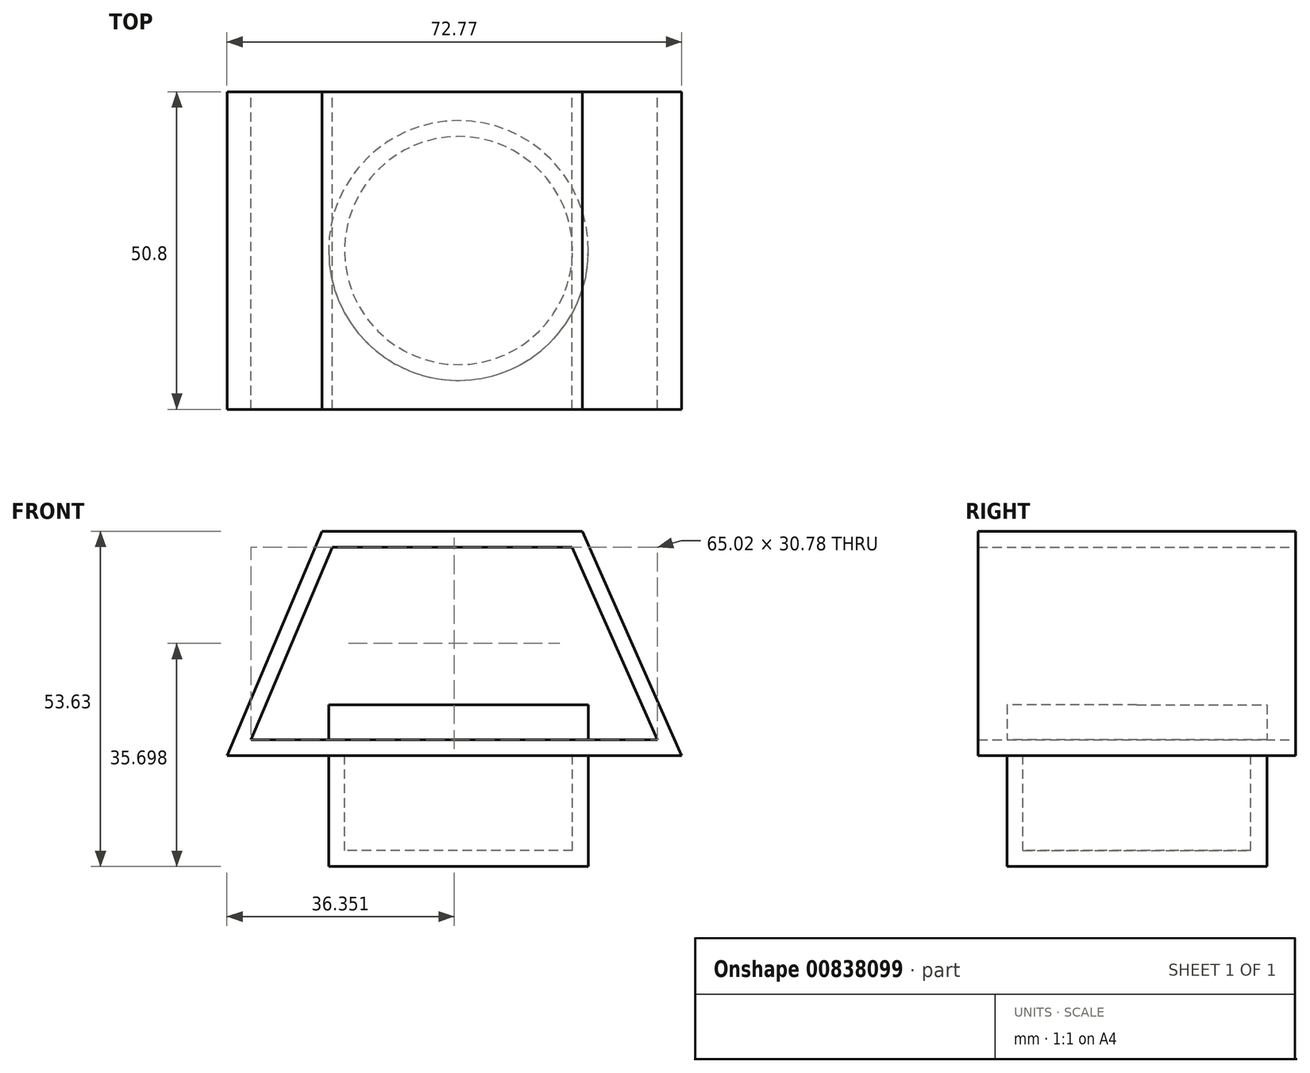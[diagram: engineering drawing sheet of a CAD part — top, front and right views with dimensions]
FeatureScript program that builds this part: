
annotation { "Feature Type Name" : "Feature", "Feature Type Description" : "" }
export const myFeature = defineFeature(function(context is Context, id is Id, definition is map)
    precondition{}
    {
        {
            var Q0;
            Q0=qCreatedBy(makeId("Front.planeOp"),FACE);
            var sketch = newSketch(context, id + "F0", { "sketchPlane" : qUnion([Q0])});
            skLineSegment(sketch, "E0", {"start": v(19.83, 35.86) * mm, "end": v(-21.85, 35.86) * mm});
            skLineSegment(sketch, "E1", {"start": v(-21.85, 35.86) * mm, "end": v(-37.05, 0) * mm});
            skLineSegment(sketch, "E2", {"start": v(19.83, 35.86) * mm, "end": v(35.72, 0) * mm});
            skLineSegment(sketch, "E3", {"start": v(35.72, 0) * mm, "end": v(0, 0) * mm});
            skLineSegment(sketch, "E4", {"start": v(0, 0) * mm, "end": v(-37.05, 0) * mm});
            skSolve(sketch);
        }
        {
            var Q0;
            Q0=makeQuery(id+"F0.imprint","IMPRINT",FACE,{"disambiguationData":[TD([[makeQuery(id+"F0.imprint","IMPRINT",EDGE,{"derivedFrom":sQuery(id+"F0.wireOp",EDGE,"E0")}),1.0]])]});
            extrude(context, id + "F1", {"entities" : qUnion([Q0]), "depth" : 25.4 * mm, "offsetDistance" : 25.4 * mm});
        }
        {
            var Q0;
            Q0=qCreatedBy(makeId("Top.planeOp"),FACE);
            var sketch = newSketch(context, id + "F2", { "sketchPlane" : qUnion([Q0])});
            skCircle(sketch, "E5", {"center": v(0, 0) * mm, "radius": 20.78 * mm});
            skSolve(sketch);
        }
        {
            var Q0;
            Q0=makeQuery(id+"F2.imprint","IMPRINT",FACE,{"disambiguationData":[TD([[makeQuery(id+"F2.imprint","IMPRINT",EDGE,{"derivedFrom":sQuery(id+"F2.wireOp",EDGE,"E5")}),1.0]])]});
            extrude(context, id + "F3", {"entities" : qUnion([Q0]), "operationType" : NewBodyOperationType.ADD, "oppositeDirection" : true, "depth" : 17.77 * mm, "offsetDistance" : 25.4 * mm});
        }
        {
            var Q0;
            Q0=makeQuery(id+"F3.opExtrude","CAP_FACE",FACE,{"disambiguationData":[OSD([sQuery(id+"F2.wireOp",EDGE,"E5")])],"isStart":true});
            extrude(context, id + "F4", {"entities" : qUnion([Q0]), "operationType" : NewBodyOperationType.ADD, "depth" : 11.56 * mm, "offsetDistance" : 25.4 * mm});
        }
        {
            var Q0;
            Q0=makeQuery(id+"F0.imprint","IMPRINT",FACE,{"disambiguationData":[TD([[makeQuery(id+"F0.imprint","IMPRINT",EDGE,{"derivedFrom":sQuery(id+"F0.wireOp",EDGE,"E0")}),1.0]])]});
            extrude(context, id + "F5", {"entities" : qUnion([Q0]), "operationType" : NewBodyOperationType.ADD, "oppositeDirection" : true, "depth" : 25.4 * mm, "offsetDistance" : 25.4 * mm});
        }
        {
            var Q0;
            Q0=makeQuery(id+"F1.opExtrude","CAP_FACE",FACE,{"disambiguationData":[OSD([sQuery(id+"F0.wireOp",EDGE,"E0"),sQuery(id+"F0.wireOp",EDGE,"E1"),sQuery(id+"F0.wireOp",EDGE,"E2"),sQuery(id+"F0.wireOp",EDGE,"E3"),sQuery(id+"F0.wireOp",EDGE,"E4")])],"isStart":false});
            var Q1;
            Q1=makeQuery(id+"F5.opExtrude","CAP_FACE",FACE,{"disambiguationData":[OSD([sQuery(id+"F0.wireOp",EDGE,"E0"),sQuery(id+"F0.wireOp",EDGE,"E1"),sQuery(id+"F0.wireOp",EDGE,"E2"),sQuery(id+"F0.wireOp",EDGE,"E3"),sQuery(id+"F0.wireOp",EDGE,"E4")])],"isStart":false});
            shell(context, id + "F6", {"entities" : qUnion([Q0, Q1]), "thickness" : 2.54 * mm});
        }
        {
            var Q0;
            Q0=makeQuery(id+"F2.imprint","IMPRINT",FACE,{"disambiguationData":[TD([[makeQuery(id+"F2.imprint","IMPRINT",EDGE,{"derivedFrom":sQuery(id+"F2.wireOp",EDGE,"E5")}),1.0]])]});
            extrude(context, id + "F7", {"entities" : qUnion([Q0]), "operationType" : NewBodyOperationType.ADD, "depth" : 8.1 * mm, "offsetDistance" : 25.4 * mm});
        }
    });
